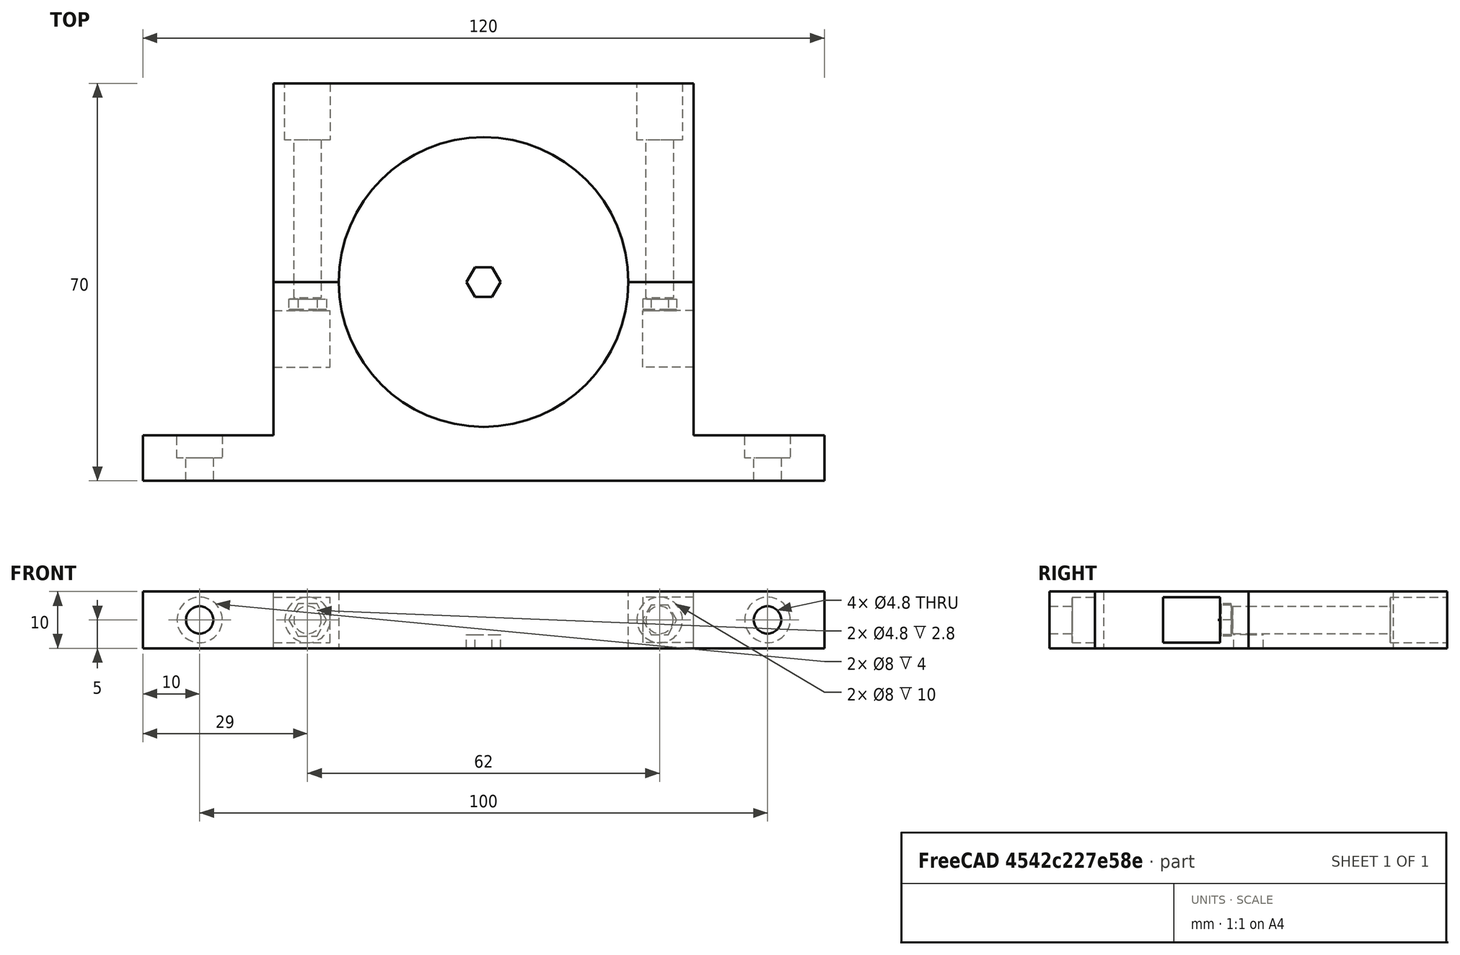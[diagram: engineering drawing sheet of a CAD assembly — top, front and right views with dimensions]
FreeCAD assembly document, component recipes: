
FREECAD ASSEMBLY — COMPONENT RECIPES ("TubeMount_CloudrayC35")

This assembly document has 4 components, labeled P0..P3 below (a component is one placed body or linked part). 0 of them carry a construction recipe — the FreeCAD feature program that regenerates the part from scratch, quoted from this document or its linked companion documents; the rest are supplied as boundary geometry only. No exploded tour is included for this assembly.
COMPONENT P0 — geometry summary ("DIN934_M4"; no construction recipe available for this part):
  bounding box: 6.6 x 5.7 x 2.6 mm
  tessellated surface: 20 triangles
  volume: 75 mm^3 (75% of its bounding box)
  symmetry: 2-fold rotationally symmetric about the x axis; 6-fold rotationally symmetric about the y axis; 2-fold rotationally symmetric about the z axis; mirror-symmetric across its x mid-plane, z mid-plane
COMPONENT P1 — geometry summary ("DIN934_M005"; no construction recipe available for this part):
  bounding box: 6.0 x 5.2 x 2.4 mm
  tessellated surface: 20 triangles
  volume: 56 mm^3 (75% of its bounding box)
  symmetry: 2-fold rotationally symmetric about the x axis; 6-fold rotationally symmetric about the y axis; 2-fold rotationally symmetric about the z axis; mirror-symmetric across its x mid-plane, z mid-plane
COMPONENT P2 — geometry summary ("DIN934_M007"; no construction recipe available for this part):
  bounding box: 6.6 x 5.7 x 2.6 mm
  tessellated surface: 20 triangles
  volume: 75 mm^3 (75% of its bounding box)
  symmetry: 2-fold rotationally symmetric about the x axis; 6-fold rotationally symmetric about the y axis; 2-fold rotationally symmetric about the z axis; mirror-symmetric across its x mid-plane, z mid-plane
COMPONENT P3 — geometry summary ("DIN934_M008"; no construction recipe available for this part):
  bounding box: 6.0 x 5.2 x 2.4 mm
  tessellated surface: 20 triangles
  volume: 56 mm^3 (75% of its bounding box)
  symmetry: 2-fold rotationally symmetric about the x axis; 6-fold rotationally symmetric about the y axis; 2-fold rotationally symmetric about the z axis; mirror-symmetric across its x mid-plane, z mid-plane
PROVENANCE & LICENSES
A FreeCAD (.FCStd) document from a public repository crawl; recipes are the document's own serialized feature recipes (and, for linked parts, companion documents' recipes).
License: bsd.
